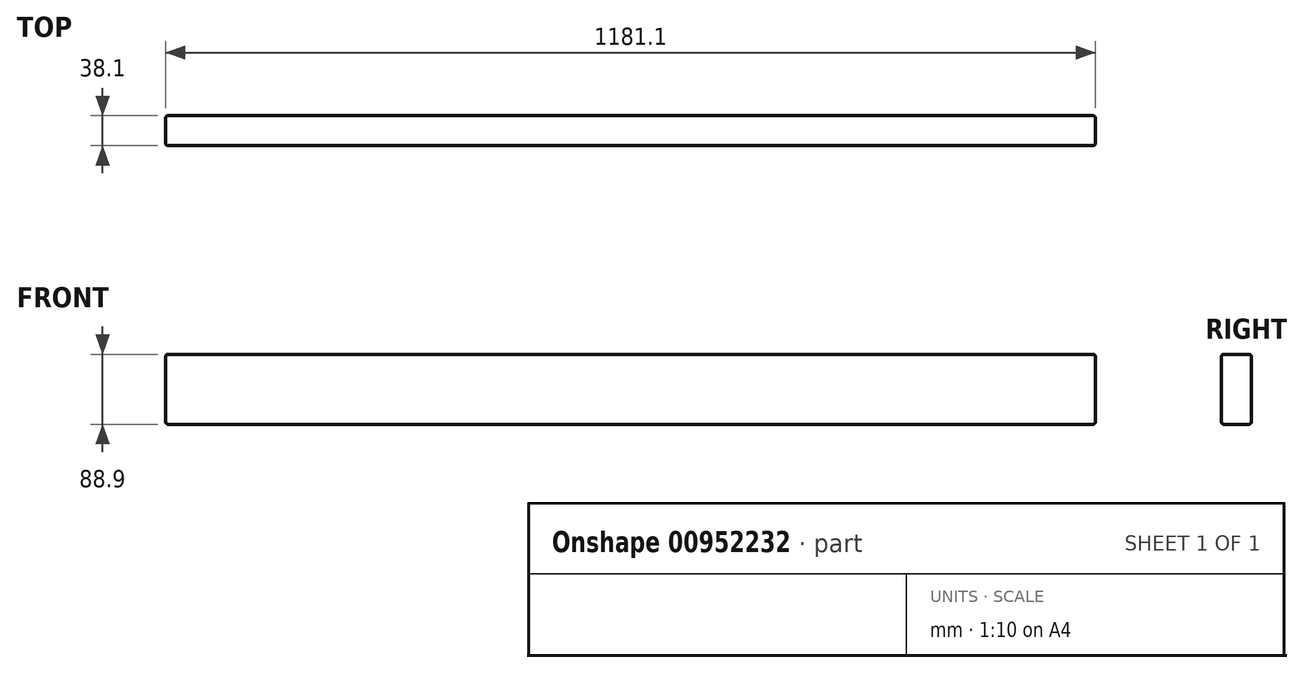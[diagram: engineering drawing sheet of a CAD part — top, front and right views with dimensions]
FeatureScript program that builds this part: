
annotation { "Feature Type Name" : "Feature", "Feature Type Description" : "" }
export const myFeature = defineFeature(function(context is Context, id is Id, definition is map)
    precondition{}
    {
        {
            var Q0;
            Q0=qCreatedBy(makeId("Front.planeOp"),FACE);
            var sketch = newSketch(context, id + "F0", { "sketchPlane" : qUnion([Q0])});
            skLineSegment(sketch, "E0.bottom", {"start": v(0, 0) * mm, "end": v(1181.1, 0) * mm});
            skLineSegment(sketch, "E0.top", {"start": v(0, -88.9) * mm, "end": v(1181.1, -88.9) * mm});
            skLineSegment(sketch, "E0.left", {"start": v(0, 0) * mm, "end": v(0, -88.9) * mm});
            skLineSegment(sketch, "E0.right", {"start": v(1181.1, 0) * mm, "end": v(1181.1, -88.9) * mm});
            skSolve(sketch);
        }
        {
            var Q0;
            Q0 = qSketchRegion(id + "F0", true);
            extrude(context, id + "F1", {"entities" : qUnion([Q0]), "depth" : 38.1 * mm, "offsetDistance" : 25.4 * mm});
        }
        {
            var Q0;
            Q0=makeQuery(id+"F1.opExtrude","CAP_EDGE",EDGE,{"disambiguationData":[OSD([sQuery(id+"F0.wireOp",EDGE,"E0.bottom")])],"isStart":true});
            var Q1;
            Q1=makeQuery(id+"F1.opExtrude","CAP_EDGE",EDGE,{"disambiguationData":[OSD([sQuery(id+"F0.wireOp",EDGE,"E0.top")])],"isStart":true});
            var Q2;
            Q2=makeQuery(id+"F1.opExtrude","CAP_EDGE",EDGE,{"disambiguationData":[OSD([sQuery(id+"F0.wireOp",EDGE,"E0.left")])],"isStart":true});
            var Q3;
            Q3=makeQuery(id+"F1.opExtrude","SWEPT_EDGE",EDGE,{"disambiguationData":[OSD([sQuery(id+"F0.wireOp",EDGE,"E0.top"),sQuery(id+"F0.wireOp",EDGE,"E0.left")])]});
            var Q4;
            Q4=makeQuery(id+"F1.opExtrude","CAP_EDGE",EDGE,{"disambiguationData":[OSD([sQuery(id+"F0.wireOp",EDGE,"E0.left")])],"isStart":false});
            var Q5;
            Q5=makeQuery(id+"F1.opExtrude","SWEPT_EDGE",EDGE,{"disambiguationData":[OSD([sQuery(id+"F0.wireOp",EDGE,"E0.bottom"),sQuery(id+"F0.wireOp",EDGE,"E0.left")])]});
            var Q6;
            Q6=makeQuery(id+"F1.opExtrude","CAP_EDGE",EDGE,{"disambiguationData":[OSD([sQuery(id+"F0.wireOp",EDGE,"E0.top")])],"isStart":false});
            var Q7;
            Q7=makeQuery(id+"F1.opExtrude","CAP_EDGE",EDGE,{"disambiguationData":[OSD([sQuery(id+"F0.wireOp",EDGE,"E0.right")])],"isStart":true});
            var Q8;
            Q8=makeQuery(id+"F1.opExtrude","SWEPT_EDGE",EDGE,{"disambiguationData":[OSD([sQuery(id+"F0.wireOp",EDGE,"E0.top"),sQuery(id+"F0.wireOp",EDGE,"E0.right")])]});
            var Q9;
            Q9=makeQuery(id+"F1.opExtrude","CAP_EDGE",EDGE,{"disambiguationData":[OSD([sQuery(id+"F0.wireOp",EDGE,"E0.bottom")])],"isStart":false});
            var Q10;
            Q10=makeQuery(id+"F1.opExtrude","CAP_EDGE",EDGE,{"disambiguationData":[OSD([sQuery(id+"F0.wireOp",EDGE,"E0.right")])],"isStart":false});
            var Q11;
            Q11=makeQuery(id+"F1.opExtrude","SWEPT_EDGE",EDGE,{"disambiguationData":[OSD([sQuery(id+"F0.wireOp",EDGE,"E0.bottom"),sQuery(id+"F0.wireOp",EDGE,"E0.right")])]});
            fillet(context, id + "F2", {"entities" : qUnion([Q0, Q1, Q2, Q3, Q4, Q5, Q6, Q7, Q8, Q9, Q10, Q11]), "radius" : 3.17 * mm, "tangentPropagation" : true, "allowEdgeOverflow" : false});
        }
    });
